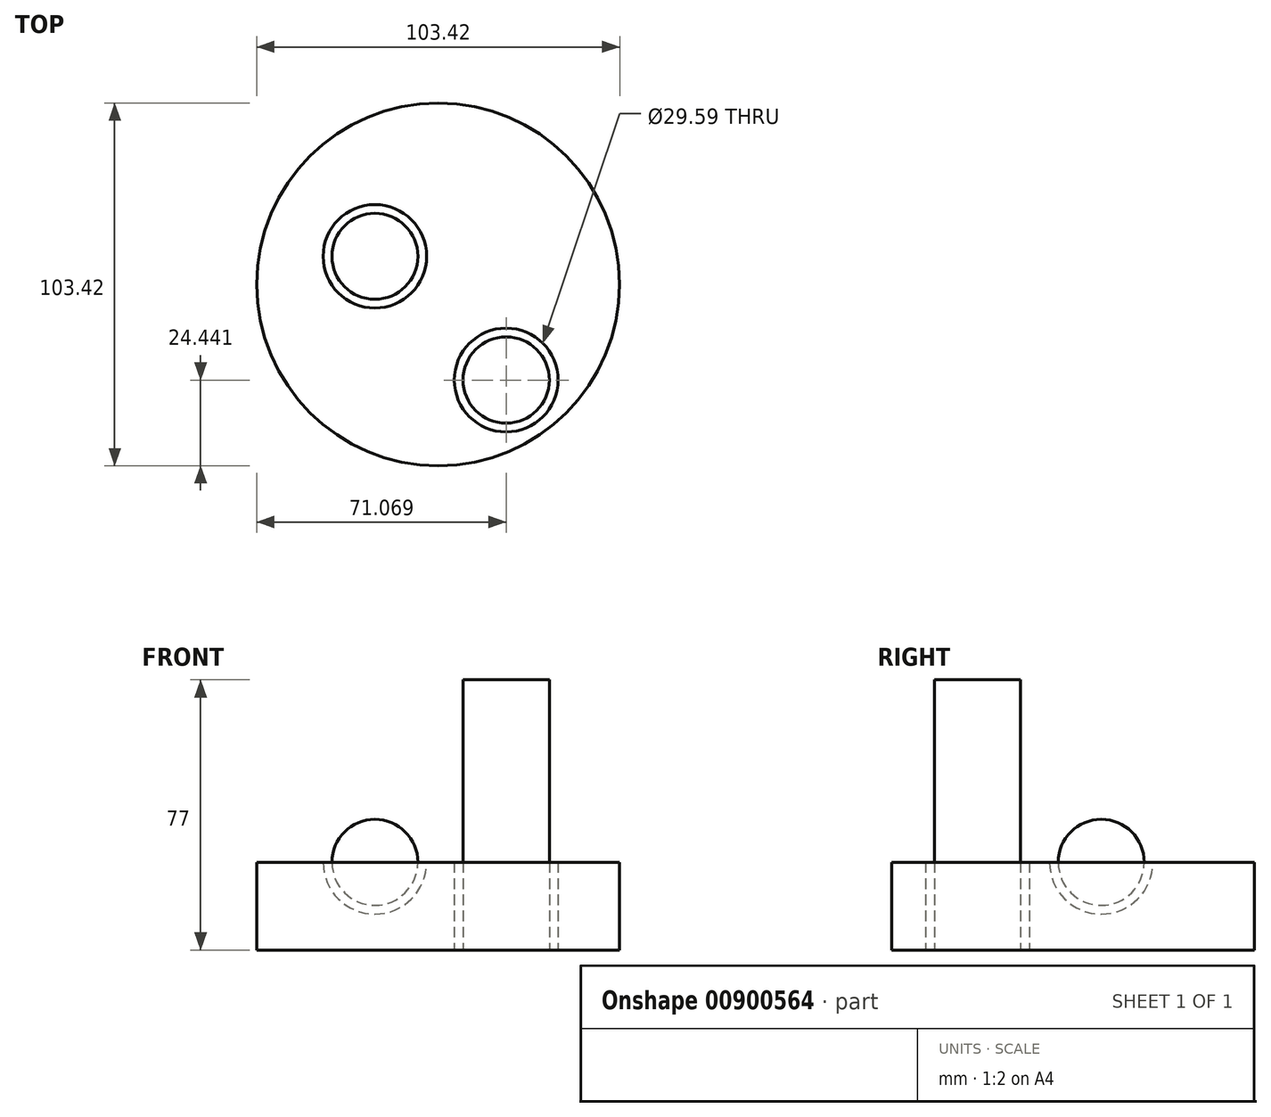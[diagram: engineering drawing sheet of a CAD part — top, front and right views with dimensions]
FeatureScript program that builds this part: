
annotation { "Feature Type Name" : "Feature", "Feature Type Description" : "" }
export const myFeature = defineFeature(function(context is Context, id is Id, definition is map)
    precondition{}
    {
        {
            var Q0;
            Q0=qCreatedBy(makeId("Top.planeOp"),FACE);
            var sketch = newSketch(context, id + "F0", { "sketchPlane" : qUnion([Q0])});
            skCircle(sketch, "E0", {"center": v(-9.8, 26.55) * mm, "radius": 12.3 * mm});
            skCircle(sketch, "E1", {"center": v(-29.16, 53.82) * mm, "radius": 51.7 * mm});
            skSolve(sketch);
        }
        {
            var Q0;
            Q0=makeQuery(id+"F0.imprint","IMPRINT",FACE,{"disambiguationData":[TD([[makeQuery(id+"F0.imprint","IMPRINT",EDGE,{"derivedFrom":sQuery(id+"F0.wireOp",EDGE,"E0")}),-1.0]])]});
            extrude(context, id + "F1", {"entities" : qUnion([Q0]), "depth" : 25 * mm, "offsetDistance" : 25 * mm});
        }
        {
            var Q0;
            Q0=makeQuery(id+"F0.imprint","IMPRINT",FACE,{"disambiguationData":[TD([[makeQuery(id+"F0.imprint","IMPRINT",EDGE,{"derivedFrom":sQuery(id+"F0.wireOp",EDGE,"E0")}),1.0]])]});
            extrude(context, id + "F2", {"entities" : qUnion([Q0]), "depth" : 77 * mm, "offsetDistance" : 25 * mm});
        }
        {
            var Q0;
            Q0=makeQuery(id+"F1.opExtrude","CAP_FACE",FACE,{"disambiguationData":[OSD([sQuery(id+"F0.wireOp",EDGE,"E0"),sQuery(id+"F0.wireOp",EDGE,"E1")])],"isStart":false});
            var sketch = newSketch(context, id + "F3", { "sketchPlane" : qUnion([Q0])});
            skArc(sketch, "E2", {"start": v(-47.23, 49.57) * mm, "mid": v(-34.98, 61.82) * mm, "end": v(-47.23, 74.07) * mm});
            skLineSegment(sketch, "E3", {"start": v(-47.23, 74.07) * mm, "end": v(-47.23, 49.57) * mm});
            skSolve(sketch);
        }
        {
            var Q0;
            Q0 = qSketchRegion(id + "F3", true);
            var Q1;
            Q1=sQuery(id+"F3.wireOp",EDGE,"E3");
            revolve(context, id + "F4", {"surfaceOperationType" : NewSurfaceOperationType.NEW, "entities" : qUnion([Q0]), "axis" : qUnion([Q1]), "revolveType" : RevolveType.FULL});
        }
        {
            var Q0;
            Q0=makeQuery(id+"F4.opRevolve","SWEPT_BODY",BODY,{"disambiguationData":[OSD([sQuery(id+"F3.wireOp",EDGE,"E2"),sQuery(id+"F3.wireOp",EDGE,"E3")])]});
            var Q1;
            Q1=makeQuery(id+"F1.opExtrude","SWEPT_BODY",BODY,{"disambiguationData":[OSD([sQuery(id+"F0.wireOp",EDGE,"E0"),sQuery(id+"F0.wireOp",EDGE,"E1")])]});
            var Q2;
            Q2=makeQuery(id+"F4.opRevolve","SWEPT_FACE",FACE,{"disambiguationData":[OSD([sQuery(id+"F3.wireOp",EDGE,"E2")])]});
            booleanBodies(context, id + "F5", {"operationType" : BooleanOperationType.SUBTRACTION, "tools" : qUnion([Q0]), "targets" : qUnion([Q1]), "offset" : true, "entitiesToOffset" : qUnion([Q2]), "offsetDistance" : 2.5 * mm, "keepTools" : true});
        }
        {
            var Q0;
            Q0=makeQuery(id+"F2.opExtrude","SWEPT_BODY",BODY,{"disambiguationData":[OSD([sQuery(id+"F0.wireOp",EDGE,"E0")])]});
            var Q1;
            Q1=makeQuery(id+"F1.opExtrude","SWEPT_BODY",BODY,{"disambiguationData":[OSD([sQuery(id+"F0.wireOp",EDGE,"E0"),sQuery(id+"F0.wireOp",EDGE,"E1")])]});
            var Q2;
            Q2=makeQuery(id+"F2.opExtrude","SWEPT_FACE",FACE,{"disambiguationData":[OSD([sQuery(id+"F0.wireOp",EDGE,"E0")])]});
            booleanBodies(context, id + "F6", {"operationType" : BooleanOperationType.SUBTRACTION, "tools" : qUnion([Q0]), "targets" : qUnion([Q1]), "offset" : true, "entitiesToOffset" : qUnion([Q2]), "offsetDistance" : 2.5 * mm, "keepTools" : true});
        }
    });
